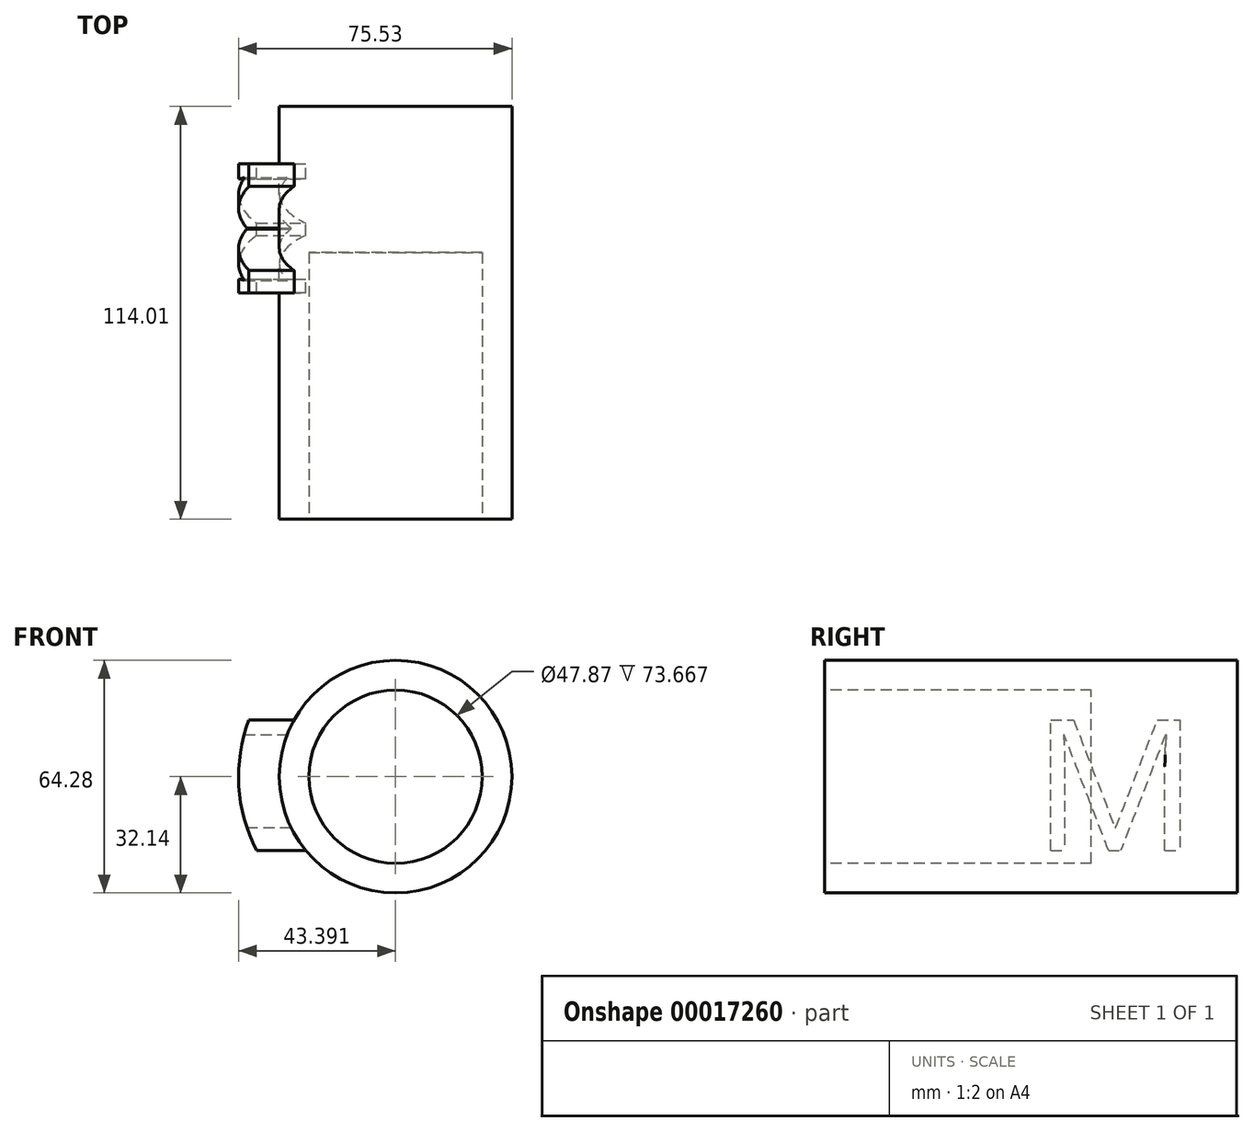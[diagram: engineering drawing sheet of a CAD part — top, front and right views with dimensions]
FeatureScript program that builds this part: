
annotation { "Feature Type Name" : "Feature", "Feature Type Description" : "" }
export const myFeature = defineFeature(function(context is Context, id is Id, definition is map)
    precondition{}
    {
        {
            var Q0;
            Q0=qCreatedBy(makeId("Front.planeOp"),FACE);
            var sketch = newSketch(context, id + "F0", { "sketchPlane" : qUnion([Q0])});
            skCircle(sketch, "E0", {"center": v(42.47, 0) * mm, "radius": 44.45 * mm});
            skSolve(sketch);
        }
        {
            var Q0;
            Q0=makeQuery(id+"F0.imprint","IMPRINT",FACE,{"disambiguationData":[TD([[makeQuery(id+"F0.imprint","IMPRINT",EDGE,{"derivedFrom":sQuery(id+"F0.wireOp",EDGE,"E0")}),1.0]])]});
            extrude(context, id + "F1", {"entities" : qUnion([Q0]), "depth" : 127.47 * mm});
        }
        {
            var Q0;
            Q0=makeQuery(id+"F1.opExtrude","CAP_FACE",FACE,{"disambiguationData":[OSD([sQuery(id+"F0.wireOp",EDGE,"E0")])],"isStart":false});
            var sketch = newSketch(context, id + "F2", { "sketchPlane" : qUnion([Q0])});
            skCircle(sketch, "E1", {"center": v(42.47, 0) * mm, "radius": 31.91 * mm});
            skSolve(sketch);
        }
        {
            var Q0;
            Q0=makeQuery(id+"F2.imprint","IMPRINT",FACE,{"disambiguationData":[TD([[makeQuery(id+"F2.imprint","IMPRINT",EDGE,{"derivedFrom":sQuery(id+"F2.wireOp",EDGE,"E1")}),1.0]])]});
            extrude(context, id + "F3", {"entities" : qUnion([Q0]), "operationType" : NewBodyOperationType.REMOVE, "oppositeDirection" : true, "depth" : 87.44 * mm});
        }
        {
            var Q0;
            Q0=qCreatedBy(makeId("Right.planeOp"),FACE);
            var sketch = newSketch(context, id + "F4", { "sketchPlane" : qUnion([Q0])});
            skText(sketch, "E2", { "text": "M", "fontName": "OpenSans-Regular.ttf"});
            const initialGuessF4  = {"E2": [-0.05653, -0.02041, 1, 0, 0.03642]};
            skSetInitialGuess(sketch, initialGuessF4);
            skSolve(sketch);
        }
        {
            var Q0;
            Q0=makeQuery(id+"F4.imprint","IMPRINT",FACE,{"disambiguationData":[TD([[makeQuery(id+"F4.imprint","IMPRINT",EDGE,{"derivedFrom":sQuery(id+"F4.wireOp",EDGE,"E2.sketch_text.stroke-0")}),-1.0]])]});
            extrude(context, id + "F5", {"entities" : qUnion([Q0]), "operationType" : NewBodyOperationType.INTERSECT, "oppositeDirection" : true, "depth" : 25.62 * mm, "hasSecondDirection" : true, "secondDirectionOppositeDirection" : false, "secondDirectionDepth" : 30.26 * mm});
        }
        {
            var Q0;
            Q0=qCreatedBy(makeId("Front.planeOp"),FACE);
            var sketch = newSketch(context, id + "F6", { "sketchPlane" : qUnion([Q0])});
            skCircle(sketch, "E3", {"center": v(41.41, 0) * mm, "radius": 32.14 * mm});
            skSolve(sketch);
        }
        {
            var Q0;
            Q0=makeQuery(id+"F6.imprint","IMPRINT",FACE,{"disambiguationData":[TD([[makeQuery(id+"F6.imprint","IMPRINT",EDGE,{"derivedFrom":sQuery(id+"F6.wireOp",EDGE,"E3")}),1.0]])]});
            extrude(context, id + "F7", {"entities" : qUnion([Q0]), "operationType" : NewBodyOperationType.ADD, "depth" : 114 * mm});
        }
        {
            var Q0;
            Q0=makeQuery(id+"F7.opExtrude","CAP_FACE",FACE,{"disambiguationData":[OSD([sQuery(id+"F6.wireOp",EDGE,"E3")])],"isStart":false});
            var sketch = newSketch(context, id + "F8", { "sketchPlane" : qUnion([Q0])});
            skCircle(sketch, "E4", {"center": v(41.41, 0) * mm, "radius": 23.94 * mm});
            skSolve(sketch);
        }
        {
            var Q0;
            Q0=makeQuery(id+"F8.imprint","IMPRINT",FACE,{"disambiguationData":[TD([[makeQuery(id+"F8.imprint","IMPRINT",EDGE,{"derivedFrom":sQuery(id+"F8.wireOp",EDGE,"E4")}),1.0]])]});
            extrude(context, id + "F9", {"entities" : qUnion([Q0]), "operationType" : NewBodyOperationType.REMOVE, "oppositeDirection" : true, "depth" : 73.67 * mm});
        }
    });
